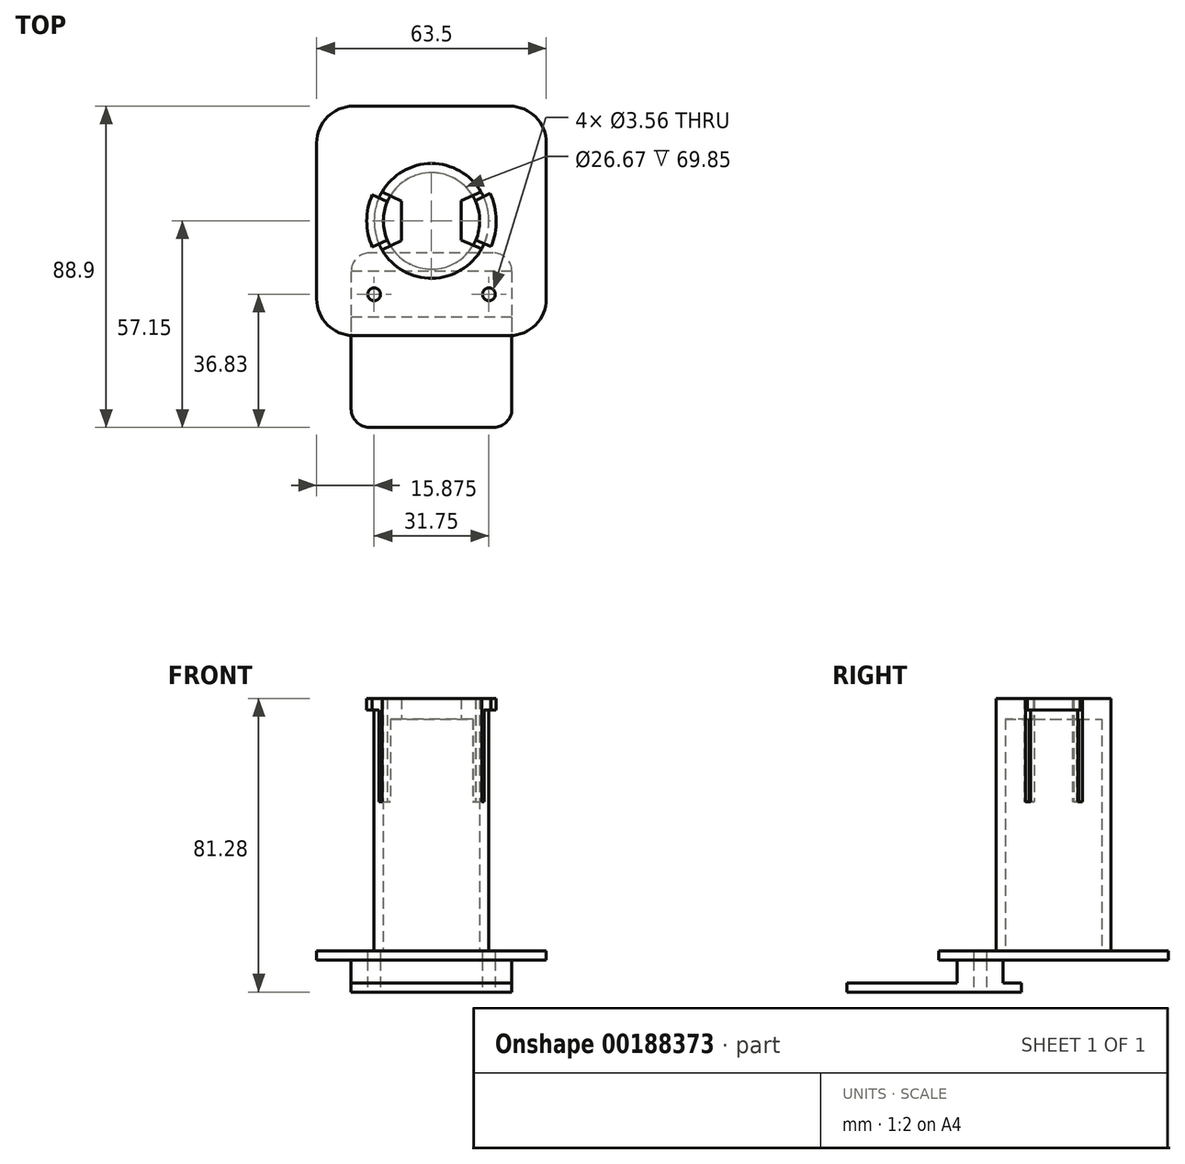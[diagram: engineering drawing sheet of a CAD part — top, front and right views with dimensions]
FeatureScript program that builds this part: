
annotation { "Feature Type Name" : "Feature", "Feature Type Description" : "" }
export const myFeature = defineFeature(function(context is Context, id is Id, definition is map)
    precondition{}
    {
        {
            var Q0;
            Q0=qCreatedBy(makeId("Top.planeOp"),FACE);
            var sketch = newSketch(context, id + "F0", { "sketchPlane" : qUnion([Q0])});
            skCircle(sketch, "E0", {"center": v(0, 0) * mm, "radius": 13.33 * mm});
            skCircle(sketch, "E1", {"center": v(0, 0) * mm, "radius": 15.88 * mm});
            skSolve(sketch);
        }
        {
            var Q0;
            Q0 = qSketchRegion(id + "F0", true);
            extrude(context, id + "F1", {"entities" : qUnion([Q0]), "depth" : 41.27 * mm});
        }
        {
            var Q0;
            Q0=makeQuery(id+"F1.opExtrude","CAP_FACE",FACE,{"disambiguationData":[OSD([sQuery(id+"F0.wireOp",EDGE,"E0"),sQuery(id+"F0.wireOp",EDGE,"E1")])],"isStart":false});
            var sketch = newSketch(context, id + "F2", { "sketchPlane" : qUnion([Q0])});
            skArc(sketch, "E2.0", {"start": v(-12.25, 5.28) * mm, "mid": v(-13.33, 0) * mm, "end": v(-12.25, -5.28) * mm});
            skArc(sketch, "E3.0", {"start": v(-14.55, 6.35) * mm, "mid": v(-15.88, 0) * mm, "end": v(-14.55, -6.35) * mm});
            skLineSegment(sketch, "E4", {"start": v(-14.55, 6.35) * mm, "end": v(-12.25, 5.28) * mm});
            skLineSegment(sketch, "E5", {"start": v(-14.55, -6.35) * mm, "end": v(-12.25, -5.28) * mm});
            skLineSegment(sketch, "E6", {"start": v(12.08, 5.64) * mm, "end": v(14.38, 6.72) * mm});
            skLineSegment(sketch, "E7", {"start": v(12.22, -5.33) * mm, "end": v(14.55, -6.35) * mm});
            skLineSegment(sketch, "E8", {"start": v(-13.69, 8.04) * mm, "end": v(-8.25, 5.52) * mm});
            skLineSegment(sketch, "E9", {"start": v(8.25, 5.54) * mm, "end": v(13.67, 8.06) * mm});
            skLineSegment(sketch, "E10", {"start": v(-13.68, -8.05) * mm, "end": v(-8.25, -5.52) * mm});
            skLineSegment(sketch, "E11", {"start": v(8.25, -5.27) * mm, "end": v(13.87, -7.72) * mm});
            skLineSegment(sketch, "E12", {"start": v(-8.25, 5.52) * mm, "end": v(-8.25, -5.52) * mm});
            skLineSegment(sketch, "E13", {"start": v(8.25, 5.54) * mm, "end": v(8.25, -5.27) * mm});
            skArc(sketch, "E14.trimOffspring", {"start": v(-11.37, -6.97) * mm, "mid": v(0.16, -13.33) * mm, "end": v(11.53, -6.7) * mm});
            skArc(sketch, "E15.trimOffspring", {"start": v(-13.68, -8.05) * mm, "mid": v(0.2, -15.87) * mm, "end": v(13.87, -7.72) * mm});
            skArc(sketch, "E16.trimOffspring", {"start": v(12.22, -5.33) * mm, "mid": v(13.33, 0.17) * mm, "end": v(12.08, 5.64) * mm});
            skArc(sketch, "E17.trimOffspring", {"start": v(14.55, -6.35) * mm, "mid": v(15.87, 0.2) * mm, "end": v(14.38, 6.72) * mm});
            skArc(sketch, "E18.trimOffspring", {"start": v(13.67, 8.06) * mm, "mid": v(-0.01, 15.87) * mm, "end": v(-13.69, 8.04) * mm});
            skArc(sketch, "E19.trimOffspring", {"start": v(11.36, 6.98) * mm, "mid": v(-0.01, 13.33) * mm, "end": v(-11.37, 6.96) * mm});
            skPoint(sketch, "E20.orphan", {"position": v(0, 1.68) * mm});
            skPoint(sketch, "E21.orphan", {"position": v(0, -1.66) * mm});
            skSolve(sketch);
        }
        {
            var Q0;
            Q0 = qSketchRegion(id + "F2", true);
            extrude(context, id + "F3", {"entities" : qUnion([Q0]), "operationType" : NewBodyOperationType.ADD, "depth" : 28.57 * mm});
        }
        {
            var Q0;
            Q0=makeQuery(id+"F3.opExtrude","CAP_FACE",FACE,{"disambiguationData":[OSD([sQuery(id+"F2.wireOp",EDGE,"E8"),sQuery(id+"F2.wireOp",EDGE,"E9"),sQuery(id+"F2.wireOp",EDGE,"E10"),sQuery(id+"F2.wireOp",EDGE,"E11"),sQuery(id+"F2.wireOp",EDGE,"E12"),sQuery(id+"F2.wireOp",EDGE,"E13"),sQuery(id+"F2.wireOp",EDGE,"E15.trimOffspring"),sQuery(id+"F2.wireOp",EDGE,"E18.trimOffspring")])],"isStart":true});
            var sketch = newSketch(context, id + "F4", { "sketchPlane" : qUnion([Q0])});
            skCircle(sketch, "E22.0", {"center": v(0, 0) * mm, "radius": 13.33 * mm});
            skSolve(sketch);
        }
        {
            var Q0;
            Q0 = qSketchRegion(id + "F4", true);
            extrude(context, id + "F5", {"entities" : qUnion([Q0]), "operationType" : NewBodyOperationType.REMOVE, "oppositeDirection" : true, "depth" : 22.86 * mm});
        }
        {
            var Q0;
            Q0=makeQuery(id+"F3.opExtrude","CAP_FACE",FACE,{"disambiguationData":[OSD([sQuery(id+"F2.wireOp",EDGE,"E8"),sQuery(id+"F2.wireOp",EDGE,"E9"),sQuery(id+"F2.wireOp",EDGE,"E10"),sQuery(id+"F2.wireOp",EDGE,"E11"),sQuery(id+"F2.wireOp",EDGE,"E12"),sQuery(id+"F2.wireOp",EDGE,"E13"),sQuery(id+"F2.wireOp",EDGE,"E15.trimOffspring"),sQuery(id+"F2.wireOp",EDGE,"E18.trimOffspring")])],"isStart":false});
            var sketch = newSketch(context, id + "F6", { "sketchPlane" : qUnion([Q0])});
            skArc(sketch, "E23", {"start": v(-16.4, 7.2) * mm, "mid": v(-17.9, 0) * mm, "end": v(-16.4, -7.2) * mm});
            skLineSegment(sketch, "E24", {"start": v(14.38, 6.72) * mm, "end": v(16.23, 7.57) * mm});
            skLineSegment(sketch, "E25", {"start": v(-14.55, 6.35) * mm, "end": v(-16.4, 7.2) * mm});
            skLineSegment(sketch, "E26", {"start": v(-14.55, -6.35) * mm, "end": v(-16.4, -7.2) * mm});
            skLineSegment(sketch, "E27", {"start": v(14.55, -6.35) * mm, "end": v(16.41, -7.16) * mm});
            skPoint(sketch, "E28.0.start.orphan", {"position": v(12.08, 5.64) * mm});
            skPoint(sketch, "E28.3.end.orphan", {"position": v(-12.25, 5.28) * mm});
            skPoint(sketch, "E28.2.end.orphan", {"position": v(-12.25, -5.28) * mm});
            skPoint(sketch, "E28.1.start.orphan", {"position": v(12.22, -5.33) * mm});
            skArc(sketch, "E29.trimOffspring", {"start": v(16.41, -7.16) * mm, "mid": v(17.9, 0.23) * mm, "end": v(16.23, 7.57) * mm});
            skArc(sketch, "E30.0", {"start": v(-14.55, 6.35) * mm, "mid": v(-15.88, 0) * mm, "end": v(-14.55, -6.35) * mm});
            skArc(sketch, "E31.0", {"start": v(14.55, -6.35) * mm, "mid": v(15.87, 0.2) * mm, "end": v(14.38, 6.72) * mm});
            skSolve(sketch);
        }
        {
            var Q0;
            Q0 = qSketchRegion(id + "F6", true);
            extrude(context, id + "F7", {"entities" : qUnion([Q0]), "operationType" : NewBodyOperationType.ADD, "oppositeDirection" : true, "depth" : 3.17 * mm});
        }
        {
            var Q0;
            Q0=makeQuery(id+"F1.opExtrude","CAP_FACE",FACE,{"disambiguationData":[OSD([sQuery(id+"F0.wireOp",EDGE,"E0"),sQuery(id+"F0.wireOp",EDGE,"E1")])],"isStart":true});
            var sketch = newSketch(context, id + "F8", { "sketchPlane" : qUnion([Q0])});
            skLineSegment(sketch, "E32.bottom", {"start": v(31.75, 31.75) * mm, "end": v(-31.75, 31.75) * mm});
            skLineSegment(sketch, "E32.top", {"start": v(31.75, -31.75) * mm, "end": v(-31.75, -31.75) * mm});
            skLineSegment(sketch, "E32.left", {"start": v(31.75, 31.75) * mm, "end": v(31.75, -31.75) * mm});
            skLineSegment(sketch, "E32.right", {"start": v(-31.75, 31.75) * mm, "end": v(-31.75, -31.75) * mm});
            skPoint(sketch, "E32.middle", {"position": v(0, 0) * mm});
            skSolve(sketch);
        }
        {
            var Q0;
            Q0 = qSketchRegion(id + "F8", true);
            extrude(context, id + "F9", {"entities" : qUnion([Q0]), "depth" : 2.54 * mm});
        }
        {
            var Q0;
            Q0=makeQuery(id+"F9.opExtrude","CAP_FACE",FACE,{"disambiguationData":[OSD([sQuery(id+"F8.wireOp",EDGE,"E32.bottom"),sQuery(id+"F8.wireOp",EDGE,"E32.top"),sQuery(id+"F8.wireOp",EDGE,"E32.left"),sQuery(id+"F8.wireOp",EDGE,"E32.right")])],"isStart":false});
            var sketch = newSketch(context, id + "F10", { "sketchPlane" : qUnion([Q0])});
            skLineSegment(sketch, "E33.bottom", {"start": v(22.22, 13.97) * mm, "end": v(-22.23, 13.97) * mm});
            skLineSegment(sketch, "E33.top", {"start": v(22.22, 26.67) * mm, "end": v(-22.23, 26.67) * mm});
            skLineSegment(sketch, "E33.left", {"start": v(22.22, 13.97) * mm, "end": v(22.22, 26.67) * mm});
            skLineSegment(sketch, "E33.right", {"start": v(-22.23, 13.97) * mm, "end": v(-22.23, 26.67) * mm});
            skPoint(sketch, "E33.middle", {"position": v(0, 20.32) * mm});
            skPoint(sketch, "E34", {"position": v(0, 31.75) * mm});
            skSolve(sketch);
        }
        {
            var Q0;
            Q0 = qSketchRegion(id + "F10", true);
            extrude(context, id + "F11", {"entities" : qUnion([Q0]), "depth" : 6.35 * mm});
        }
        {
            var Q0;
            Q0=makeQuery(id+"F11.opExtrude","CAP_FACE",FACE,{"disambiguationData":[OSD([sQuery(id+"F10.wireOp",EDGE,"E33.bottom"),sQuery(id+"F10.wireOp",EDGE,"E33.top"),sQuery(id+"F10.wireOp",EDGE,"E33.left"),sQuery(id+"F10.wireOp",EDGE,"E33.right")])],"isStart":false});
            var sketch = newSketch(context, id + "F12", { "sketchPlane" : qUnion([Q0])});
            skLineSegment(sketch, "E35.bottom", {"start": v(22.22, 8.9) * mm, "end": v(-22.23, 8.89) * mm});
            skLineSegment(sketch, "E35.top", {"start": v(22.23, 57.15) * mm, "end": v(-22.22, 57.15) * mm});
            skLineSegment(sketch, "E35.left", {"start": v(22.22, 8.89) * mm, "end": v(22.23, 57.15) * mm});
            skLineSegment(sketch, "E35.right", {"start": v(-22.23, 8.9) * mm, "end": v(-22.22, 57.15) * mm});
            skPoint(sketch, "E35.middle", {"position": v(0, 33.02) * mm});
            skPoint(sketch, "E35.middle.positionSnap0", {"position": v(0, 26.67) * mm});
            skPoint(sketch, "E35.centerSnap0", {"position": v(0, 26.67) * mm});
            skSolve(sketch);
        }
        {
            var Q0;
            Q0 = qSketchRegion(id + "F12", true);
            extrude(context, id + "F13", {"entities" : qUnion([Q0]), "operationType" : NewBodyOperationType.ADD, "depth" : 2.54 * mm});
        }
        {
            var Q0;
            Q0=makeQuery(id+"F13.opExtrude","SWEPT_EDGE",EDGE,{"disambiguationData":[OSD([sQuery(id+"F12.wireOp",EDGE,"E35.top"),sQuery(id+"F12.wireOp",EDGE,"E35.left")])]});
            var Q1;
            Q1=makeQuery(id+"F13.opExtrude","SWEPT_EDGE",EDGE,{"disambiguationData":[OSD([sQuery(id+"F12.wireOp",EDGE,"E35.top"),sQuery(id+"F12.wireOp",EDGE,"E35.right")])]});
            var Q2;
            Q2=makeQuery(id+"F13.opExtrude","SWEPT_EDGE",EDGE,{"disambiguationData":[OSD([sQuery(id+"F12.wireOp",EDGE,"E35.bottom"),sQuery(id+"F12.wireOp",EDGE,"E35.left")])]});
            var Q3;
            Q3=makeQuery(id+"F13.opExtrude","SWEPT_EDGE",EDGE,{"disambiguationData":[OSD([sQuery(id+"F12.wireOp",EDGE,"E35.bottom"),sQuery(id+"F12.wireOp",EDGE,"E35.right")])]});
            fillet(context, id + "F14", {"entities" : qUnion([Q0, Q1, Q2, Q3]), "radius" : 5.08 * mm, "tangentPropagation" : true, "allowEdgeOverflow" : false});
        }
        {
            var Q0;
            Q0=makeQuery(id+"F9.opExtrude","SWEPT_EDGE",EDGE,{"disambiguationData":[OSD([sQuery(id+"F8.wireOp",EDGE,"E32.bottom"),sQuery(id+"F8.wireOp",EDGE,"E32.right")])]});
            var Q1;
            Q1=makeQuery(id+"F9.opExtrude","SWEPT_EDGE",EDGE,{"disambiguationData":[OSD([sQuery(id+"F8.wireOp",EDGE,"E32.top"),sQuery(id+"F8.wireOp",EDGE,"E32.right")])]});
            var Q2;
            Q2=makeQuery(id+"F9.opExtrude","SWEPT_EDGE",EDGE,{"disambiguationData":[OSD([sQuery(id+"F8.wireOp",EDGE,"E32.top"),sQuery(id+"F8.wireOp",EDGE,"E32.left")])]});
            var Q3;
            Q3=makeQuery(id+"F9.opExtrude","SWEPT_EDGE",EDGE,{"disambiguationData":[OSD([sQuery(id+"F8.wireOp",EDGE,"E32.bottom"),sQuery(id+"F8.wireOp",EDGE,"E32.left")])]});
            fillet(context, id + "F15", {"entities" : qUnion([Q0, Q1, Q2, Q3]), "radius" : 10.16 * mm, "tangentPropagation" : true, "allowEdgeOverflow" : false});
        }
        {
            var Q0;
            Q0=makeQuery(id+"F13.opExtrude","CAP_FACE",FACE,{"disambiguationData":[OSD([sQuery(id+"F12.wireOp",EDGE,"E35.bottom"),sQuery(id+"F12.wireOp",EDGE,"E35.top"),sQuery(id+"F12.wireOp",EDGE,"E35.left"),sQuery(id+"F12.wireOp",EDGE,"E35.right")])],"isStart":false});
            var sketch = newSketch(context, id + "F16", { "sketchPlane" : qUnion([Q0])});
            skCircle(sketch, "E36", {"center": v(15.87, 20.32) * mm, "radius": 1.78 * mm});
            skCircle(sketch, "E37", {"center": v(-15.88, 20.32) * mm, "radius": 1.78 * mm});
            skSolve(sketch);
        }
        {
            var Q0;
            Q0 = qSketchRegion(id + "F16", true);
            var Q1;
            Q1=makeQuery(id+"F9.opExtrude","CAP_FACE",FACE,{"disambiguationData":[OSD([sQuery(id+"F8.wireOp",EDGE,"E32.bottom"),sQuery(id+"F8.wireOp",EDGE,"E32.top"),sQuery(id+"F8.wireOp",EDGE,"E32.left"),sQuery(id+"F8.wireOp",EDGE,"E32.right")])],"isStart":true});
            extrude(context, id + "F17", {"entities" : qUnion([Q0]), "operationType" : NewBodyOperationType.REMOVE, "endBound" : BoundingType.UP_TO_SURFACE, "oppositeDirection" : true, "endBoundEntityFace" : qUnion([Q1]), "depth" : 25.4 * mm});
        }
        {
            var Q0;
            Q0=makeQuery(id+"F9.opExtrude","CAP_FACE",FACE,{"disambiguationData":[OSD([sQuery(id+"F8.wireOp",EDGE,"E32.bottom"),sQuery(id+"F8.wireOp",EDGE,"E32.top"),sQuery(id+"F8.wireOp",EDGE,"E32.left"),sQuery(id+"F8.wireOp",EDGE,"E32.right")])],"isStart":true});
            var sketch = newSketch(context, id + "F18", { "sketchPlane" : qUnion([Q0])});
            skCircle(sketch, "E38.0", {"center": v(-15.88, -20.32) * mm, "radius": 1.78 * mm});
            skCircle(sketch, "E39.0", {"center": v(15.87, -20.32) * mm, "radius": 1.78 * mm});
            skSolve(sketch);
        }
        {
            var Q0;
            Q0 = qSketchRegion(id + "F18", true);
            extrude(context, id + "F19", {"entities" : qUnion([Q0]), "operationType" : NewBodyOperationType.REMOVE, "oppositeDirection" : true, "depth" : 25.4 * mm});
        }
    });
